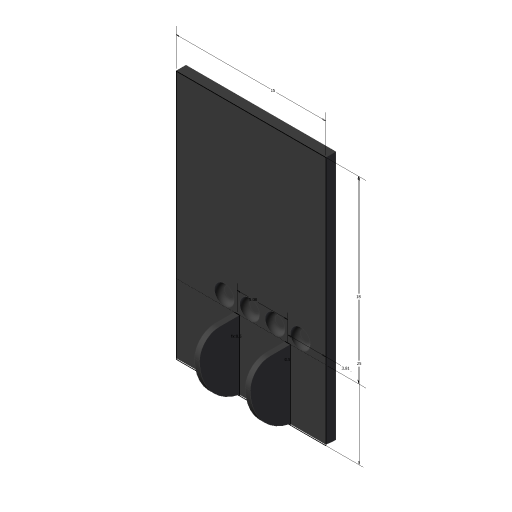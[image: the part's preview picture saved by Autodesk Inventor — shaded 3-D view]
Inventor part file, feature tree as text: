
AUTODESK INVENTOR PART (.ipt)
format: ipt  version: 2023 (Build 270158000, 158)  size: 151,552 bytes
history: native  units: mm
features: extrude x3, fillet x3, sketch x2, projected_geometry x1
ambient origin geometry x8: Origin, YZ Plane, XZ Plane, XY Plane, X Axis, Y Axis, Z Axis, Center Point
bodies: Solid1 (feature_tree)
feature tree (9):
  sketch  "Sketch1"  dims[d0=15.0mm d1=25.0mm]
  extrude  "Extrusion1"  Depth=25.0mm
  extrude  "Extrusion2"  Depth=2.0mm
  extrude  "Extrusion3"  Depth=0.5mm
  fillet  "Fillet1"  Radius=0.5mm
  fillet  "Fillet2"  Radius=5.08mm
  fillet  "Fillet3"  Radius=1.0mm
  sketch  "Sketch2"  dims[d2=18.0mm d3=3.81mm d4=0.5mm d5=0.5mm d6=5.08mm d7=1.0mm d8=0.0mm d9=4.0mm d10=0.0mm d11=2.0mm d12=2.54mm d13=1.0mm d14=40.0mm d16=2.54mm d17=10.0mm d19=10.0mm d21=0.5mm d22=0.0mm d23=0.5mm d24=5.0mm d25=2.0mm]
  projected_geometry  "Projected Loop1"
